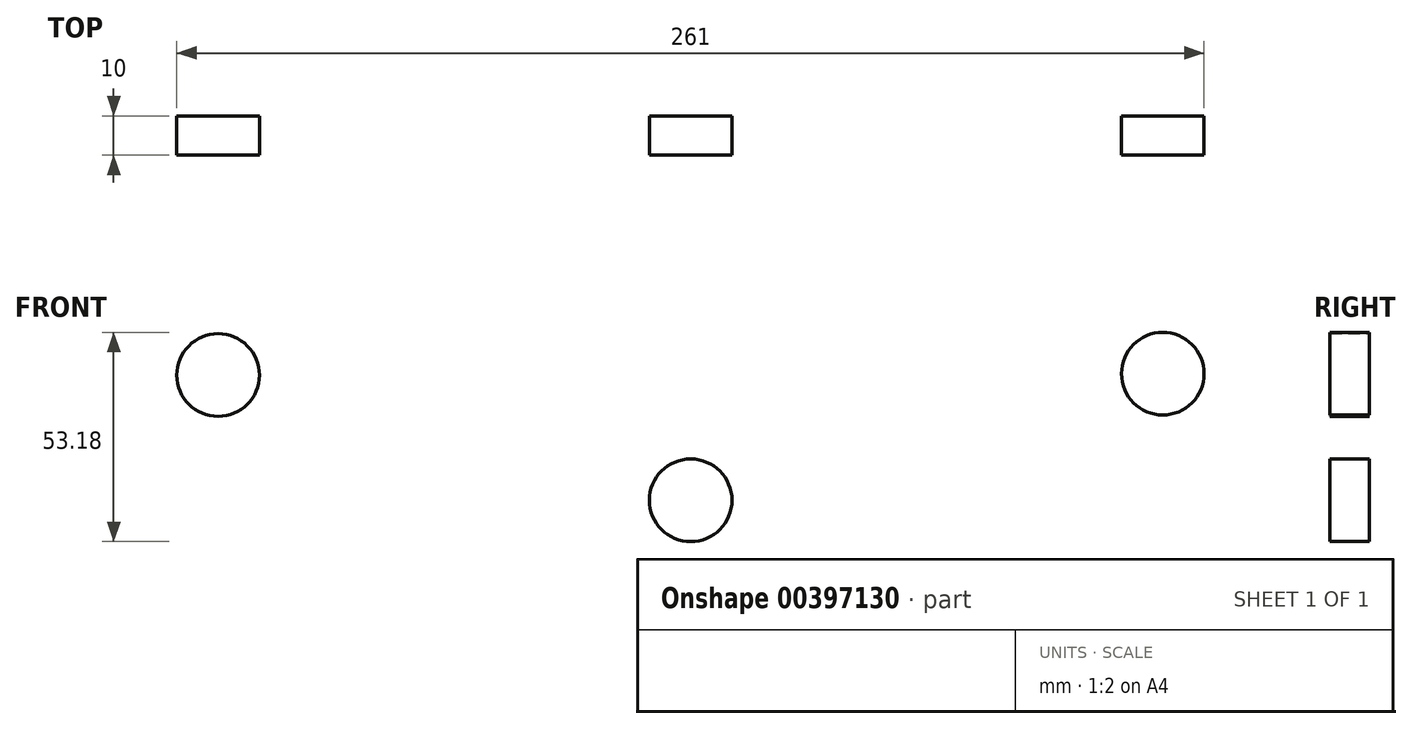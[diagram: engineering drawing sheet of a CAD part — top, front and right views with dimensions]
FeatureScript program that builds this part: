
annotation { "Feature Type Name" : "Feature", "Feature Type Description" : "" }
export const myFeature = defineFeature(function(context is Context, id is Id, definition is map)
    precondition{}
    {
        {
            var Q0;
            Q0=qCreatedBy(makeId("Front.planeOp"),FACE);
            var sketch = newSketch(context, id + "F0", { "sketchPlane" : qUnion([Q0])});
            skLineSegment(sketch, "E0", {"start": v(-118.75, 42.45) * mm, "end": v(-98.76, 42.46) * mm});
            skLineSegment(sketch, "E1", {"start": v(131.16, 42.38) * mm, "end": v(111.82, 42.35) * mm});
            skArc(sketch, "E2", {"start": v(-98.76, 42.46) * mm, "mid": v(6.51, 7.2) * mm, "end": v(111.82, 42.35) * mm});
            skCircle(sketch, "E3", {"center": v(126.24, 12.37) * mm, "radius": 10.5 * mm});
            skLineSegment(sketch, "E4", {"start": v(-133.74, 27.44) * mm, "end": v(-133.71, 2.13) * mm});
            skLineSegment(sketch, "E5", {"start": v(146.29, 2.13) * mm, "end": v(146.18, 27.44) * mm});
            skPoint(sketch, "E6.visualSharp", {"position": v(-133.76, 42.45) * mm});
            skArc(sketch, "E7.filletArc", {"start": v(-118.75, 42.45) * mm, "mid": v(-129.35, 38.05) * mm, "end": v(-133.74, 27.44) * mm});
            skArc(sketch, "E8.filletArc", {"start": v(146.18, 27.44) * mm, "mid": v(141.76, 38.01) * mm, "end": v(131.16, 42.38) * mm});
            skArc(sketch, "E9.0", {"start": v(-133.71, -9.5) * mm, "mid": v(-110.3, -17.06) * mm, "end": v(-85.71, -16.03) * mm});
            skArc(sketch, "E10.0", {"start": v(98.29, -15.76) * mm, "mid": v(122.85, -16.92) * mm, "end": v(146.29, -9.5) * mm});
            skLineSegment(sketch, "E11", {"start": v(-133.71, 2.13) * mm, "end": v(-133.71, -9.5) * mm});
            skLineSegment(sketch, "E12", {"start": v(146.29, 2.13) * mm, "end": v(146.29, -9.5) * mm});
            skLineSegment(sketch, "E13", {"start": v(-133.74, 27.44) * mm, "end": v(146.18, 27.44) * mm, "construction": true});
            skLineSegment(sketch, "E14", {"start": v(6.22, 27.44) * mm, "end": v(6.33, -42.56) * mm, "construction": true});
            skCircle(sketch, "E15", {"center": v(6.3, -19.8) * mm, "radius": 10.5 * mm});
            skLineSegment(sketch, "E16.bottom", {"start": v(51.79, -67.74) * mm, "end": v(-39.21, -67.87) * mm});
            skArc(sketch, "E17.trimOffspring", {"start": v(67.85, -31.15) * mm, "mid": v(83.45, -24.22) * mm, "end": v(98.29, -15.76) * mm});
            skLineSegment(sketch, "E18", {"start": v(51.79, -67.74) * mm, "end": v(51.79, -35.15) * mm});
            skLineSegment(sketch, "E19", {"start": v(51.79, -35.15) * mm, "end": v(51.83, -31.74) * mm});
            skLineSegment(sketch, "E20", {"start": v(51.83, -31.74) * mm, "end": v(67.85, -31.15) * mm});
            skArc(sketch, "E21.MirrorCS", {"start": v(-55.23, -31.34) * mm, "mid": v(-70.86, -24.45) * mm, "end": v(-85.71, -16.03) * mm});
            skLineSegment(sketch, "E22.MirrorCS", {"start": v(-39.21, -31.87) * mm, "end": v(-55.23, -31.34) * mm});
            skLineSegment(sketch, "E23.MirrorCS", {"start": v(-39.16, -35.29) * mm, "end": v(-39.21, -31.87) * mm});
            skLineSegment(sketch, "E24.MirrorCS", {"start": v(-39.06, -67.87) * mm, "end": v(-39.16, -35.29) * mm});
            skPoint(sketch, "E25.MirrorP", {"position": v(-113.76, 12.02) * mm});
            skCircle(sketch, "E26", {"center": v(-113.76, 12.02) * mm, "radius": 10.5 * mm});
            skSolve(sketch);
        }
        {
            var Q0;
            Q0 = qSketchRegion(id + "F0", true);
            extrude(context, id + "F1", {"entities" : qUnion([Q0]), "depth" : 10 * mm, "offsetDistance" : 25 * mm});
        }
    });
